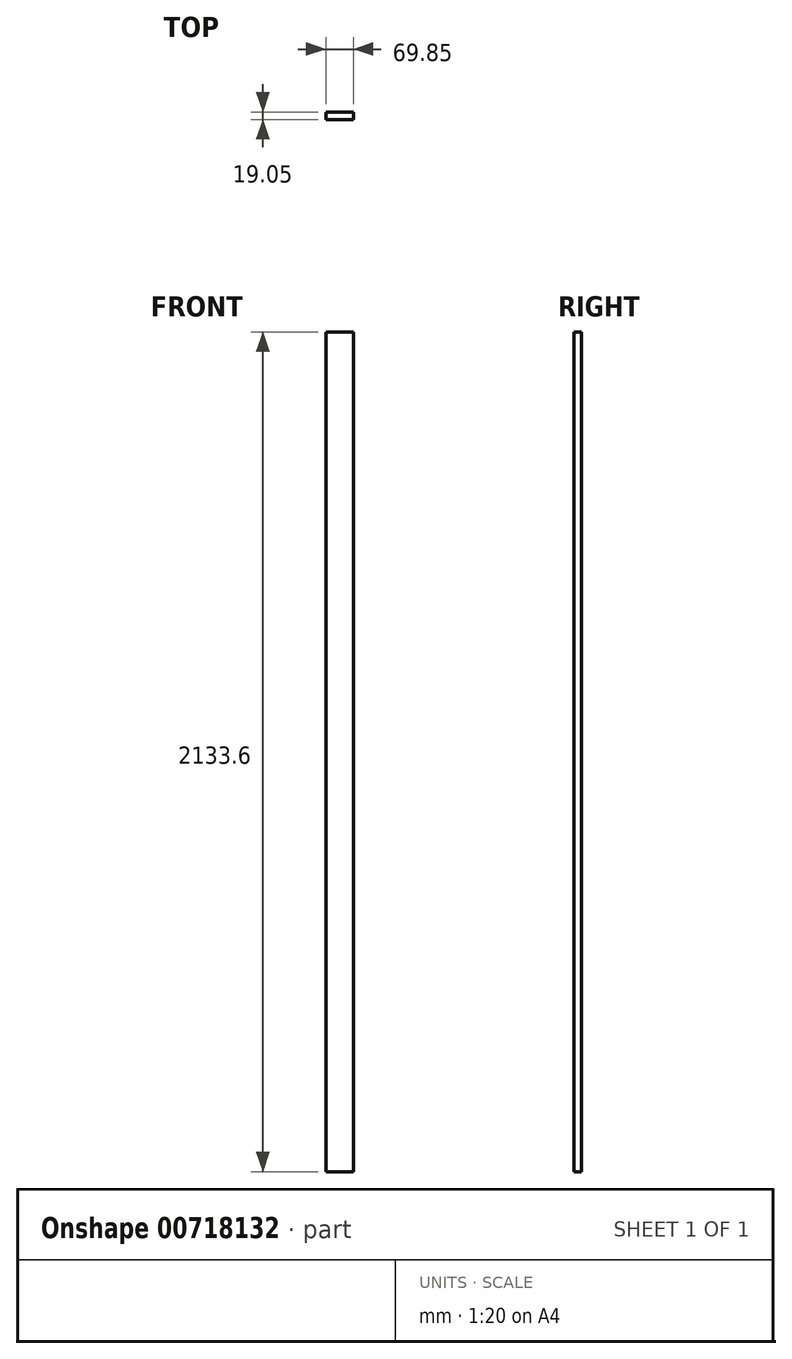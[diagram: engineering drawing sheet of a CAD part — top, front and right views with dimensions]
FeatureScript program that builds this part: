
annotation { "Feature Type Name" : "Feature", "Feature Type Description" : "" }
export const myFeature = defineFeature(function(context is Context, id is Id, definition is map)
    precondition{}
    {
        {
            var Q0;
            Q0=qCreatedBy(makeId("Front.planeOp"),FACE);
            var sketch = newSketch(context, id + "F0", { "sketchPlane" : qUnion([Q0])});
            skLineSegment(sketch, "E0.bottom", {"start": v(0, 0) * mm, "end": v(69.85, 0) * mm});
            skLineSegment(sketch, "E0.top", {"start": v(0, 2133.6) * mm, "end": v(69.85, 2133.6) * mm});
            skLineSegment(sketch, "E0.left", {"start": v(0, 0) * mm, "end": v(0, 2133.6) * mm});
            skLineSegment(sketch, "E0.right", {"start": v(69.85, 0) * mm, "end": v(69.85, 2133.6) * mm});
            skSolve(sketch);
        }
        {
            var Q0;
            Q0=makeQuery(id+"F0.imprint","IMPRINT",FACE,{"disambiguationData":[TD([[makeQuery(id+"F0.imprint","IMPRINT",EDGE,{"derivedFrom":sQuery(id+"F0.wireOp",EDGE,"E0.bottom")}),1.0]])]});
            extrude(context, id + "F1", {"entities" : qUnion([Q0]), "depth" : 19.05 * mm, "offsetDistance" : 25.4 * mm});
        }
    });
